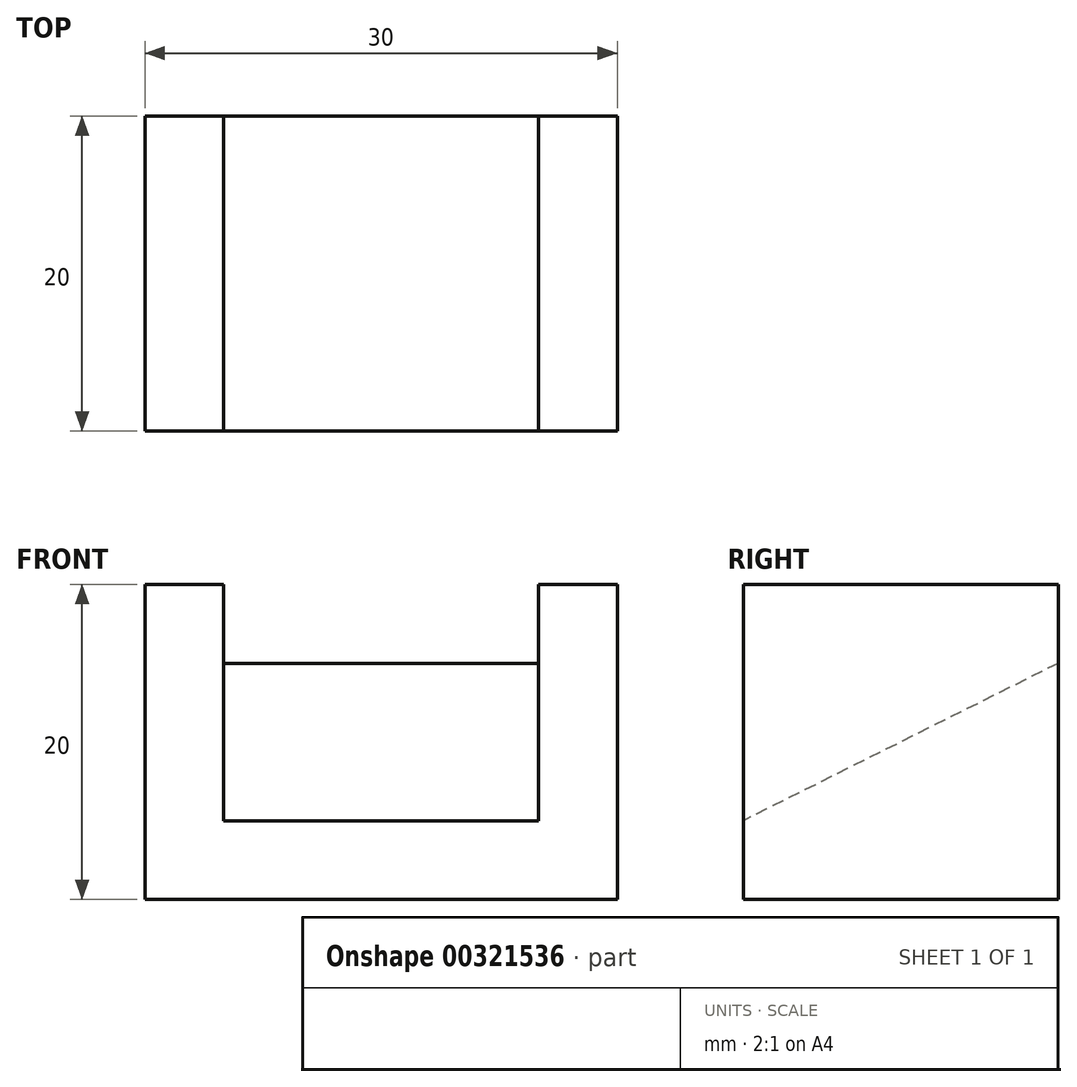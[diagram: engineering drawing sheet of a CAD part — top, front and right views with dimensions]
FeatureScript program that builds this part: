
annotation { "Feature Type Name" : "Feature", "Feature Type Description" : "" }
export const myFeature = defineFeature(function(context is Context, id is Id, definition is map)
    precondition{}
    {
        {
            var Q0;
            Q0=qCreatedBy(makeId("Right.planeOp"),FACE);
            var sketch = newSketch(context, id + "F0", { "sketchPlane" : qUnion([Q0])});
            skLineSegment(sketch, "E0", {"start": v(0, 0) * mm, "end": v(20, 0) * mm});
            skLineSegment(sketch, "E1", {"start": v(20, 0) * mm, "end": v(20, 10) * mm});
            skLineSegment(sketch, "E2", {"start": v(20, 10) * mm, "end": v(0, 0) * mm});
            skSolve(sketch);
        }
        {
            var Q0;
            Q0 = qSketchRegion(id + "F0", true);
            extrude(context, id + "F1", {"entities" : qUnion([Q0]), "endBound" : BoundingType.SYMMETRIC, "depth" : 20 * mm});
        }
        {
            var Q0;
            Q0=makeQuery(id+"F1.opExtrude","CAP_FACE",FACE,{"disambiguationData":[OSD([sQuery(id+"F0.wireOp",EDGE,"E0"),sQuery(id+"F0.wireOp",EDGE,"E1"),sQuery(id+"F0.wireOp",EDGE,"E2")])],"isStart":false});
            var sketch = newSketch(context, id + "F2", { "sketchPlane" : qUnion([Q0])});
            skLineSegment(sketch, "E3", {"start": v(20, 0) * mm, "end": v(20, 15) * mm});
            skLineSegment(sketch, "E4", {"start": v(20, 15) * mm, "end": v(0, 15) * mm});
            skLineSegment(sketch, "E5", {"start": v(0, 15) * mm, "end": v(0, 0) * mm});
            skLineSegment(sketch, "E6", {"start": v(0, 0) * mm, "end": v(20, 0) * mm});
            skSolve(sketch);
        }
        {
            var Q0;
            Q0 = qSketchRegion(id + "F2", true);
            extrude(context, id + "F3", {"entities" : qUnion([Q0]), "operationType" : NewBodyOperationType.ADD, "depth" : 5 * mm});
        }
        {
            var Q0;
            Q0=makeQuery(id+"F1.opExtrude","CAP_FACE",FACE,{"disambiguationData":[OSD([sQuery(id+"F0.wireOp",EDGE,"E0"),sQuery(id+"F0.wireOp",EDGE,"E1"),sQuery(id+"F0.wireOp",EDGE,"E2")])],"isStart":true});
            var sketch = newSketch(context, id + "F4", { "sketchPlane" : qUnion([Q0])});
            skLineSegment(sketch, "E7", {"start": v(-20, 0) * mm, "end": v(0, 0) * mm});
            skLineSegment(sketch, "E8", {"start": v(0, 0) * mm, "end": v(0, 15) * mm});
            skLineSegment(sketch, "E9", {"start": v(0, 15) * mm, "end": v(-20, 15) * mm});
            skLineSegment(sketch, "E10", {"start": v(-20, 15) * mm, "end": v(-20, 0) * mm});
            skSolve(sketch);
        }
        {
            var Q0;
            Q0 = qSketchRegion(id + "F4", true);
            extrude(context, id + "F5", {"entities" : qUnion([Q0]), "operationType" : NewBodyOperationType.ADD, "depth" : 5 * mm});
        }
        {
            var Q0;
            Q0=makeQuery(id+"F5.boolean.opBoolean","MERGE",FACE,{"derivedFrom":[makeQuery(id+"F3.boolean.opBoolean","MERGE",FACE,{"derivedFrom":[makeQuery(id+"F1.opExtrude","SWEPT_FACE",FACE,{"disambiguationData":[OSD([sQuery(id+"F0.wireOp",EDGE,"E0")])]}),makeQuery(id+"F3.opExtrude","SWEPT_FACE",FACE,{"disambiguationData":[OSD([sQuery(id+"F2.wireOp",EDGE,"E6")])]})]}),makeQuery(id+"F5.opExtrude","SWEPT_FACE",FACE,{"disambiguationData":[OSD([sQuery(id+"F4.wireOp",EDGE,"E7")])]})]});
            extrude(context, id + "F6", {"entities" : qUnion([Q0]), "operationType" : NewBodyOperationType.ADD, "depth" : 5 * mm});
        }
    });
